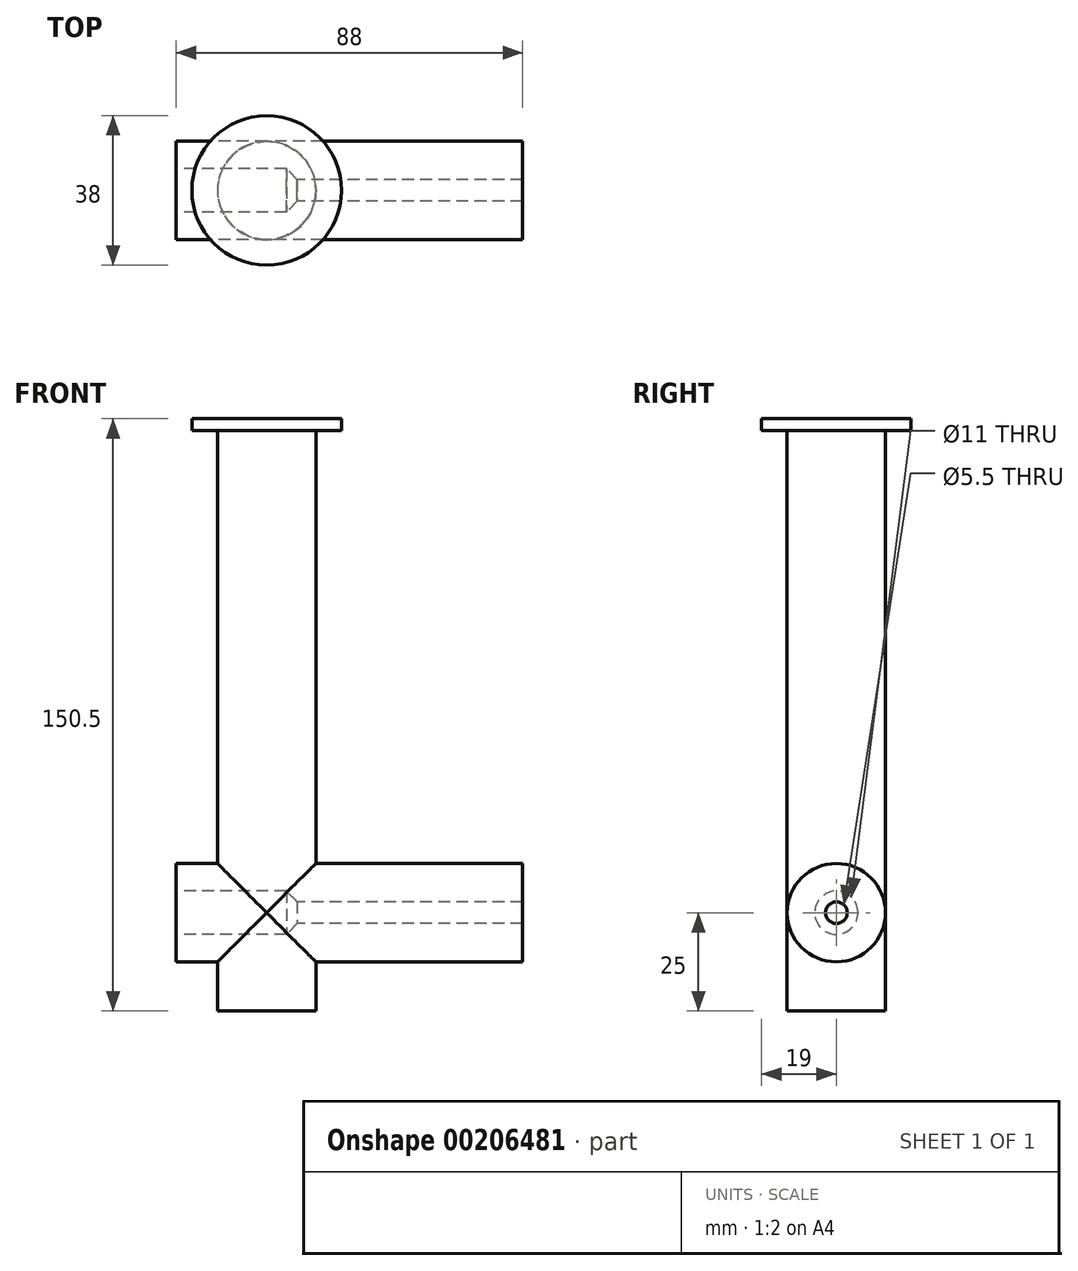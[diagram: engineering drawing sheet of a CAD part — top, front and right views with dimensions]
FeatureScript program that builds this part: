
annotation { "Feature Type Name" : "Feature", "Feature Type Description" : "" }
export const myFeature = defineFeature(function(context is Context, id is Id, definition is map)
    precondition{}
    {
        {
            var Q0;
            Q0=qCreatedBy(makeId("Top.planeOp"),FACE);
            var sketch = newSketch(context, id + "F0", { "sketchPlane" : qUnion([Q0])});
            skCircle(sketch, "E0", {"center": v(0, 0) * mm, "radius": 12.5 * mm});
            skSolve(sketch);
        }
        {
            var Q0;
            Q0 = qSketchRegion(id + "F0", true);
            extrude(context, id + "F1", {"entities" : qUnion([Q0]), "depth" : 122.5 * mm, "offsetDistance" : 25 * mm});
        }
        {
            var Q0;
            Q0=qCreatedBy(makeId("Right.planeOp"),FACE);
            var sketch = newSketch(context, id + "F2", { "sketchPlane" : qUnion([Q0])});
            skCircle(sketch, "E1", {"center": v(0, 0) * mm, "radius": 12.5 * mm});
            skSolve(sketch);
        }
        {
            var Q0;
            Q0 = qSketchRegion(id + "F2", true);
            extrude(context, id + "F3", {"entities" : qUnion([Q0]), "operationType" : NewBodyOperationType.ADD, "depth" : 65 * mm, "offsetDistance" : 25 * mm});
        }
        {
            var Q0;
            Q0 = qSketchRegion(id + "F2", true);
            extrude(context, id + "F4", {"entities" : qUnion([Q0]), "operationType" : NewBodyOperationType.ADD, "oppositeDirection" : true, "depth" : 23 * mm, "offsetDistance" : 25 * mm});
        }
        {
            var Q0;
            Q0 = qSketchRegion(id + "F0", true);
            extrude(context, id + "F5", {"entities" : qUnion([Q0]), "operationType" : NewBodyOperationType.ADD, "oppositeDirection" : true, "depth" : 25 * mm, "offsetDistance" : 25 * mm});
        }
        {
            var Q0;
            Q0=makeQuery(id+"F1.opExtrude","CAP_FACE",FACE,{"disambiguationData":[OSD([sQuery(id+"F0.wireOp",EDGE,"E0")])],"isStart":false});
            var sketch = newSketch(context, id + "F6", { "sketchPlane" : qUnion([Q0])});
            skCircle(sketch, "E2", {"center": v(0, 0) * mm, "radius": 19 * mm});
            skSolve(sketch);
        }
        {
            var Q0;
            Q0 = qSketchRegion(id + "F6", true);
            extrude(context, id + "F7", {"entities" : qUnion([Q0]), "operationType" : NewBodyOperationType.ADD, "depth" : 3 * mm, "offsetDistance" : 25 * mm});
        }
        {
            var Q0;
            Q0=makeQuery(id+"F4.opExtrude","CAP_FACE",FACE,{"disambiguationData":[OSD([sQuery(id+"F2.wireOp",EDGE,"E1")])],"isStart":false});
            var sketch = newSketch(context, id + "F8", { "sketchPlane" : qUnion([Q0])});
            skPoint(sketch, "E3", {"position": v(0, 0) * mm});
            skCircle(sketch, "E4", {"center": v(0, 0) * mm, "radius": 5.5 * mm});
            skSolve(sketch);
        }
        {
            var Q0;
            Q0=makeQuery(id+"F8.imprint","IMPRINT",FACE,{"disambiguationData":[TD([[makeQuery(id+"F8.imprint","IMPRINT",EDGE,{"derivedFrom":sQuery(id+"F8.wireOp",EDGE,"E4")}),1.0]])]});
            extrude(context, id + "F9", {"entities" : qUnion([Q0]), "operationType" : NewBodyOperationType.REMOVE, "oppositeDirection" : true, "depth" : 28 * mm, "offsetDistance" : 25 * mm});
        }
        {
            var Q0;
            Q0=makeQuery(id+"F9.boolean.opBoolean","COPY",FACE,{"derivedFrom":makeQuery(id+"F9.opExtrude","CAP_FACE",FACE,{"disambiguationData":[OSD([sQuery(id+"F8.wireOp",EDGE,"E4")])],"isStart":false})});
            var sketch = newSketch(context, id + "F10", { "sketchPlane" : qUnion([Q0])});
            skPoint(sketch, "E5", {"position": v(0, 0) * mm});
            skSolve(sketch);
        }
        {
            var Q0;
            Q0=sQuery(id+"F10.wireOp",VERTEX,"E5");
            var Q1;
            Q1=makeQuery(id+"F1.opExtrude","SWEPT_BODY",BODY,{"disambiguationData":[OSD([sQuery(id+"F0.wireOp",EDGE,"E0")])]});
            hole(context, id + "F11", {"style" : HoleStyle.C_SINK, "endStyle" : HoleEndStyle.BLIND, "holeDiameter" : 5.5 * mm, "cSinkDiameter" : 11 * mm, "cSinkAngle" : 90 * degree, "majorDiameter" : 5 * mm, "holeDepth" : 100 * mm, "isTappedThrough" : true, "tappedDepth" : 12 * mm, "tapClearance" : 3, "locations" : qUnion([Q0]), "scope" : qUnion([Q1])});
        }
    });
